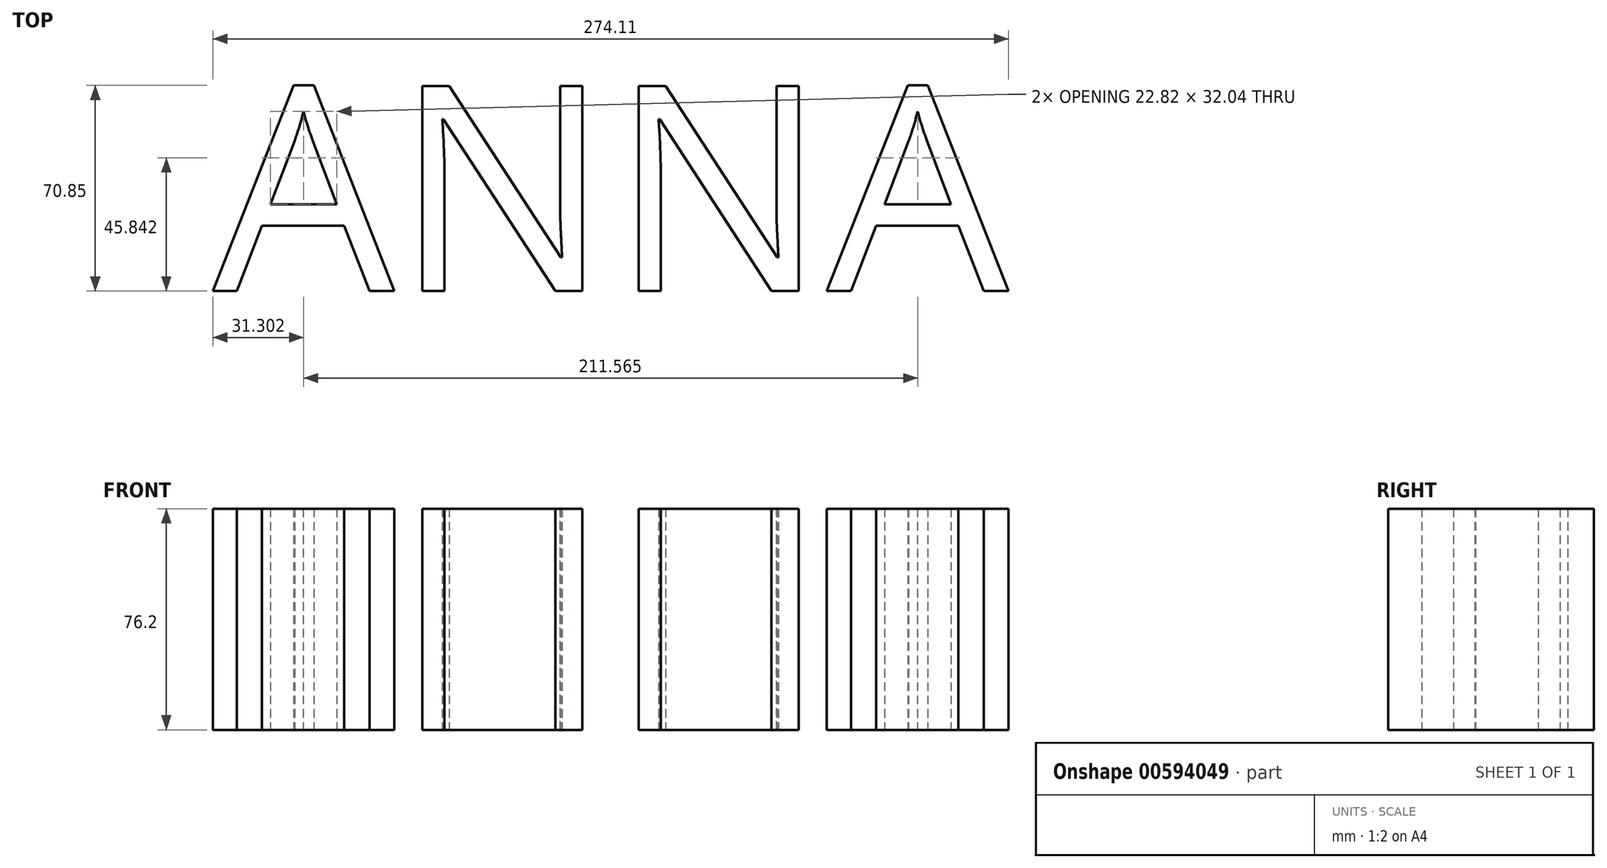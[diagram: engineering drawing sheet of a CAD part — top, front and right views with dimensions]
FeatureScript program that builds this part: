
annotation { "Feature Type Name" : "Feature", "Feature Type Description" : "" }
export const myFeature = defineFeature(function(context is Context, id is Id, definition is map)
    precondition{}
    {
        {
            var Q0;
            Q0=qCreatedBy(makeId("Top.planeOp"),FACE);
            var sketch = newSketch(context, id + "F0", { "sketchPlane" : qUnion([Q0])});
            skText(sketch, "E0", { "text": "ANNA\n", "fontName": "OpenSans-Regular.ttf"});
            const initialGuessF0  = {"E0": [-0.0259, -0.03438, 1, 0, 0.07116]};
            skSetInitialGuess(sketch, initialGuessF0);
            skSolve(sketch);
        }
        {
            var Q0;
            Q0 = qSketchRegion(id + "F0", true);
            extrude(context, id + "F1", {"entities" : qUnion([Q0]), "depth" : 76.2 * mm, "offsetDistance" : 25.4 * mm});
        }
    });
